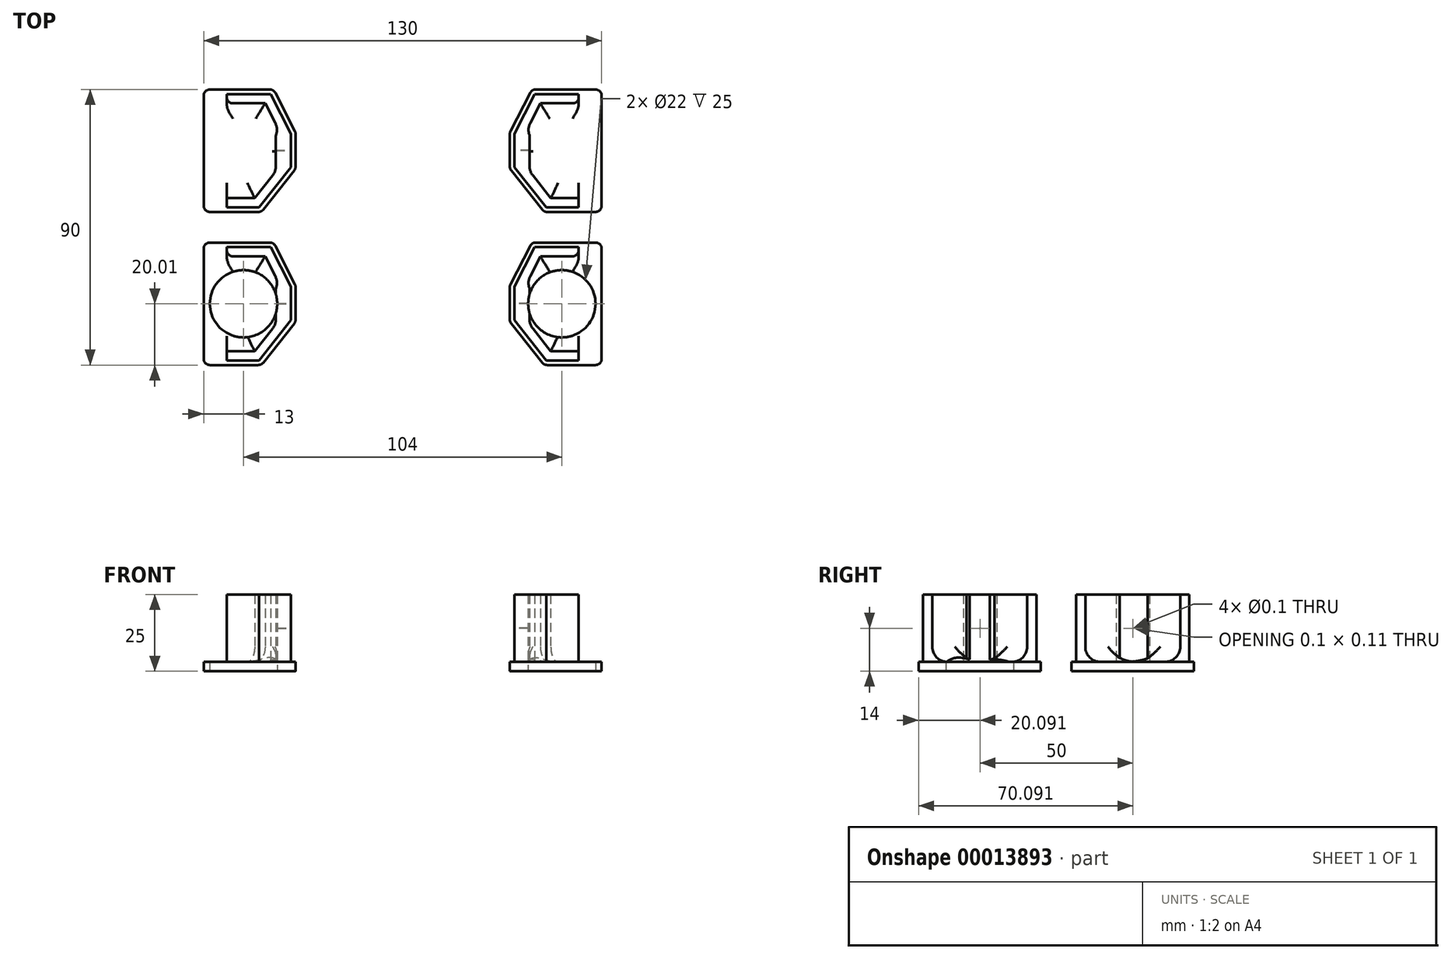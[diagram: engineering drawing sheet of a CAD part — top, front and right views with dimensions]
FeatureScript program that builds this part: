
annotation { "Feature Type Name" : "Feature", "Feature Type Description" : "" }
export const myFeature = defineFeature(function(context is Context, id is Id, definition is map)
    precondition{}
    {
        {
            var Q0;
            Q0=qCreatedBy(makeId("Right.planeOp"),FACE);
            var sketch = newSketch(context, id + "F0", { "sketchPlane" : qUnion([Q0])});
            skLineSegment(sketch, "E0", {"start": v(-20.01, 30) * mm, "end": v(-20.01, 11.2) * mm});
            skLineSegment(sketch, "E1", {"start": v(-20.01, 11.2) * mm, "end": v(-5.9, 0) * mm});
            skLineSegment(sketch, "E2", {"start": v(-5.9, 0) * mm, "end": v(5.9, 0) * mm});
            skLineSegment(sketch, "E3", {"start": v(5.9, 0) * mm, "end": v(20, 7.2) * mm});
            skLineSegment(sketch, "E4", {"start": v(20, 7.2) * mm, "end": v(19.99, 30) * mm});
            skLineSegment(sketch, "E5", {"start": v(19.99, 30) * mm, "end": v(18.49, 30) * mm});
            skLineSegment(sketch, "E6", {"start": v(18.49, 30) * mm, "end": v(18.49, 28.6) * mm});
            skLineSegment(sketch, "E7", {"start": v(18.49, 28.6) * mm, "end": v(17.7, 28.6) * mm});
            skLineSegment(sketch, "E8", {"start": v(17.7, 28.6) * mm, "end": v(16.3, 24.7) * mm});
            skLineSegment(sketch, "E9", {"start": v(18.49, 22.5) * mm, "end": v(18.49, 8.12) * mm});
            skLineSegment(sketch, "E10", {"start": v(18.49, 8.12) * mm, "end": v(5.54, 1.5) * mm});
            skLineSegment(sketch, "E11", {"start": v(5.54, 1.5) * mm, "end": v(-5.38, 1.5) * mm});
            skLineSegment(sketch, "E12", {"start": v(-5.38, 1.5) * mm, "end": v(-18.5, 11.92) * mm});
            skLineSegment(sketch, "E13", {"start": v(-18.5, 22.5) * mm, "end": v(-16.31, 24.7) * mm});
            skLineSegment(sketch, "E14", {"start": v(-16.31, 24.7) * mm, "end": v(-17.73, 28.6) * mm});
            skLineSegment(sketch, "E15", {"start": v(-17.73, 28.6) * mm, "end": v(-18.5, 28.6) * mm});
            skLineSegment(sketch, "E16", {"start": v(-18.5, 28.6) * mm, "end": v(-18.5, 30) * mm});
            skLineSegment(sketch, "E17", {"start": v(-18.5, 30) * mm, "end": v(-20.01, 30) * mm});
            skLineSegment(sketch, "E18", {"start": v(-16.31, 10.1) * mm, "end": v(-16.31, 24.7) * mm, "construction": true});
            skLineSegment(sketch, "E19", {"start": v(-18.5, 22.5) * mm, "end": v(18.49, 22.5) * mm});
            skLineSegment(sketch, "E20", {"start": v(-18.5, 22.5) * mm, "end": v(-18.5, 11.92) * mm});
            skLineSegment(sketch, "E21", {"start": v(-20.01, 30) * mm, "end": v(19.99, 30) * mm});
            skLineSegment(sketch, "E22", {"start": v(-18.5, 28.6) * mm, "end": v(18.49, 28.6) * mm, "construction": true});
            skLineSegment(sketch, "E23", {"start": v(16.29, 24.7) * mm, "end": v(18.49, 22.5) * mm});
            skLineSegment(sketch, "E24", {"start": v(-16.31, 24.7) * mm, "end": v(16.3, 24.7) * mm, "construction": true});
            skLineSegment(sketch, "E25", {"start": v(-0.01, 24.7) * mm, "end": v(-0.01, 30) * mm, "construction": true});
            skPoint(sketch, "E26", {"position": v(0, 0) * mm});
            skSolve(sketch);
        }
        {
            var Q0;
            {var subQ4=sQuery(id+"F0.wireOp",EDGE,"E0");Q0=makeQuery(id+"F0.imprint","IMPRINT",FACE,{"disambiguationData":[TD([[makeQuery(id+"F0.imprint","IMPRINT",EDGE,{"derivedFrom":subQ4}),1.0]])]});}
            var Q1;
            {var subQ2=sQuery(id+"F0.wireOp",EDGE,"E6");Q1=makeQuery(id+"F0.imprint","IMPRINT",FACE,{"disambiguationData":[TD([[makeQuery(id+"F0.imprint","IMPRINT",EDGE,{"derivedFrom":subQ2}),-1.0]])]});}
            var Q2;
            Q2=makeQuery(id+"F0.imprint","IMPRINT",FACE,{"disambiguationData":[TD([[makeQuery(id+"F0.imprint","IMPRINT",EDGE,{"derivedFrom":sQuery(id+"F0.wireOp",EDGE,"E9")}),-1.0]])]});
            extrude(context, id + "F1", {"entities" : qUnion([Q0, Q1, Q2]), "depth" : 3 * mm});
        }
        {
            var Q0;
            Q0=makeQuery(id+"F0.imprint","IMPRINT",FACE,{"disambiguationData":[TD([[makeQuery(id+"F0.imprint","IMPRINT",EDGE,{"derivedFrom":sQuery(id+"F0.wireOp",EDGE,"E9")}),-1.0]])]});
            extrude(context, id + "F2", {"entities" : qUnion([Q0]), "operationType" : NewBodyOperationType.ADD, "oppositeDirection" : true, "depth" : 22 * mm});
        }
        {
            var Q0;
            Q0=makeQuery(id+"F2.opExtrude","CAP_FACE",FACE,{"disambiguationData":[OSD([sQuery(id+"F0.wireOp",EDGE,"E9"),sQuery(id+"F0.wireOp",EDGE,"E10"),sQuery(id+"F0.wireOp",EDGE,"E11"),sQuery(id+"F0.wireOp",EDGE,"E12"),sQuery(id+"F0.wireOp",EDGE,"E19"),sQuery(id+"F0.wireOp",EDGE,"E20")])],"isStart":false});
            shell(context, id + "F3", {"entities" : qUnion([Q0]), "thickness" : 3 * mm});
        }
        {
            var Q0;
            Q0=makeQuery(id+"F3.opShell","OFFSET_FACE",FACE,{"disambiguationData":[OSD([sQuery(id+"F0.wireOp",EDGE,"E19")])]});
            extrude(context, id + "F4", {"entities" : qUnion([Q0]), "operationType" : NewBodyOperationType.REMOVE, "endBound" : BoundingType.UP_TO_NEXT, "oppositeDirection" : true, "depth" : 25 * mm});
        }
        {
            var Q0;
            Q0=makeQuery(id+"F2.opExtrude","SWEPT_FACE",FACE,{"disambiguationData":[OSD([sQuery(id+"F0.wireOp",EDGE,"E11")])]});
            var sketch = newSketch(context, id + "F5", { "sketchPlane" : qUnion([Q0])});
            skLineSegment(sketch, "E27", {"start": v(-11, 5.38) * mm, "end": v(-11, -5.54) * mm, "construction": true});
            skPoint(sketch, "E28", {"position": v(-11, -0.08) * mm});
            skSolve(sketch);
        }
        {
            var Q0;
            Q0=sQuery(id+"F5.wireOp",VERTEX,"E28");
            var Q1;
            Q1=makeQuery(id+"F1.opExtrude","SWEPT_BODY",BODY,{"disambiguationData":[OSD([sQuery(id+"F0.wireOp",EDGE,"E0"),sQuery(id+"F0.wireOp",EDGE,"E1"),sQuery(id+"F0.wireOp",EDGE,"E2"),sQuery(id+"F0.wireOp",EDGE,"E3"),sQuery(id+"F0.wireOp",EDGE,"E4"),sQuery(id+"F0.wireOp",EDGE,"E21")])]});
            hole(context, id + "F6", {"style" : HoleStyle.SIMPLE, "holeDiameter" : 1 / 203.2 * mm + 0.1 * mm, "endStyle" : HoleEndStyle.THROUGH, "locations" : qUnion([Q0]), "scope" : qUnion([Q1]), "isTappedThrough" : true});
        }
        {
            var Q0;
            Q0=makeQuery(id+"F3.opShell","OFFSET_FACE",FACE,{"disambiguationData":[OSD([sQuery(id+"F0.wireOp",EDGE,"E11")])]});
            extrude(context, id + "F7", {"entities" : qUnion([Q0]), "operationType" : NewBodyOperationType.ADD, "depth" : 2 * mm});
        }
        {
            var Q0;
            {var subQ0=sQuery(id+"F0.wireOp",EDGE,"E21");var subQ1=sQuery(id+"F0.wireOp",EDGE,"E9");var subQ2=sQuery(id+"F0.wireOp",EDGE,"E4");var subQ3=sQuery(id+"F0.wireOp",EDGE,"E3");var subQ4=sQuery(id+"F0.wireOp",EDGE,"E2");var subQ5=sQuery(id+"F0.wireOp",EDGE,"E1");var subQ6=sQuery(id+"F0.wireOp",EDGE,"E0");Q0=makeQuery(id+"F4.boolean.opBoolean","MERGE",EDGE,{"derivedFrom":[makeQuery(id+"F3.opShell","TWEAK_EDGE",EDGE,{"derivedFrom":[makeQuery(id+"F1.opExtrude","CAP_FACE",FACE,{"disambiguationData":[OSD([subQ6,subQ5,subQ4,subQ3,subQ2,subQ0])],"isStart":false}),makeQuery(id+"F2.opExtrude","SWEPT_FACE",FACE,{"disambiguationData":[OSD([subQ1])]})]})],"fromTools":[makeQuery(id+"F4.opExtrude","SWEPT_EDGE",EDGE,{"disambiguationData":[OSD([subQ6,subQ5,subQ4,subQ3,subQ2,subQ1,sQuery(id+"F0.wireOp",EDGE,"E19"),subQ0])]})]});}
            var Q1;
            Q1=makeQuery(id+"F3.opShell","TWEAK_EDGE",EDGE,{"derivedFrom":[makeQuery(id+"F1.opExtrude","CAP_FACE",FACE,{"disambiguationData":[OSD([sQuery(id+"F0.wireOp",EDGE,"E0"),sQuery(id+"F0.wireOp",EDGE,"E1"),sQuery(id+"F0.wireOp",EDGE,"E2"),sQuery(id+"F0.wireOp",EDGE,"E3"),sQuery(id+"F0.wireOp",EDGE,"E4"),sQuery(id+"F0.wireOp",EDGE,"E21")])],"isStart":false}),makeQuery(id+"F2.opExtrude","SWEPT_FACE",FACE,{"disambiguationData":[OSD([sQuery(id+"F0.wireOp",EDGE,"E10")])]})]});
            var Q2;
            Q2=makeQuery(id+"F3.opShell","TWEAK_EDGE",EDGE,{"derivedFrom":[makeQuery(id+"F1.opExtrude","CAP_FACE",FACE,{"disambiguationData":[OSD([sQuery(id+"F0.wireOp",EDGE,"E0"),sQuery(id+"F0.wireOp",EDGE,"E1"),sQuery(id+"F0.wireOp",EDGE,"E2"),sQuery(id+"F0.wireOp",EDGE,"E3"),sQuery(id+"F0.wireOp",EDGE,"E4"),sQuery(id+"F0.wireOp",EDGE,"E21")])],"isStart":false}),makeQuery(id+"F2.opExtrude","SWEPT_FACE",FACE,{"disambiguationData":[OSD([sQuery(id+"F0.wireOp",EDGE,"E11")])]})]});
            var Q3;
            Q3=makeQuery(id+"F3.opShell","TWEAK_EDGE",EDGE,{"derivedFrom":[makeQuery(id+"F1.opExtrude","CAP_FACE",FACE,{"disambiguationData":[OSD([sQuery(id+"F0.wireOp",EDGE,"E0"),sQuery(id+"F0.wireOp",EDGE,"E1"),sQuery(id+"F0.wireOp",EDGE,"E2"),sQuery(id+"F0.wireOp",EDGE,"E3"),sQuery(id+"F0.wireOp",EDGE,"E4"),sQuery(id+"F0.wireOp",EDGE,"E21")])],"isStart":false}),makeQuery(id+"F2.opExtrude","SWEPT_FACE",FACE,{"disambiguationData":[OSD([sQuery(id+"F0.wireOp",EDGE,"E12")])]})]});
            var Q4;
            {var subQ0=sQuery(id+"F0.wireOp",EDGE,"E21");var subQ1=sQuery(id+"F0.wireOp",EDGE,"E20");var subQ2=sQuery(id+"F0.wireOp",EDGE,"E4");var subQ3=sQuery(id+"F0.wireOp",EDGE,"E3");var subQ4=sQuery(id+"F0.wireOp",EDGE,"E2");var subQ5=sQuery(id+"F0.wireOp",EDGE,"E1");var subQ6=sQuery(id+"F0.wireOp",EDGE,"E0");Q4=makeQuery(id+"F4.boolean.opBoolean","MERGE",EDGE,{"derivedFrom":[makeQuery(id+"F3.opShell","TWEAK_EDGE",EDGE,{"derivedFrom":[makeQuery(id+"F1.opExtrude","CAP_FACE",FACE,{"disambiguationData":[OSD([subQ6,subQ5,subQ4,subQ3,subQ2,subQ0])],"isStart":false}),makeQuery(id+"F2.opExtrude","SWEPT_FACE",FACE,{"disambiguationData":[OSD([subQ1])]})]})],"fromTools":[makeQuery(id+"F4.opExtrude","SWEPT_EDGE",EDGE,{"disambiguationData":[OSD([subQ6,subQ5,subQ4,subQ3,subQ2,sQuery(id+"F0.wireOp",EDGE,"E19"),subQ1,subQ0])]})]});}
            fillet(context, id + "F8", {"entities" : qUnion([Q0, Q1, Q2, Q3, Q4]), "radius" : 5 * mm, "tangentPropagation" : true, "allowEdgeOverflow" : false});
        }
        {
            var Q0;
            Q0=makeQuery(id+"F4.boolean.opBoolean","COPY",EDGE,{"derivedFrom":makeQuery(id+"F4.opExtrude","CAP_EDGE",EDGE,{"disambiguationData":[OSD([sQuery(id+"F0.wireOp",EDGE,"E9"),sQuery(id+"F0.wireOp",EDGE,"E19"),sQuery(id+"F0.wireOp",EDGE,"E23")])],"isStart":false})});
            var Q1;
            Q1=makeQuery(id+"F4.boolean.opBoolean","COPY",EDGE,{"derivedFrom":makeQuery(id+"F4.opExtrude","CAP_EDGE",EDGE,{"disambiguationData":[OSD([sQuery(id+"F0.wireOp",EDGE,"E13"),sQuery(id+"F0.wireOp",EDGE,"E19"),sQuery(id+"F0.wireOp",EDGE,"E20")])],"isStart":false})});
            fillet(context, id + "F9", {"entities" : qUnion([Q0, Q1]), "radius" : 2 * mm, "tangentPropagation" : true, "allowEdgeOverflow" : false});
        }
        {
            var Q0;
            {var subQ0=sQuery(id+"F0.wireOp",EDGE,"E11");var subQ1=sQuery(id+"F0.wireOp",EDGE,"E10");Q0=makeQuery(id+"F7.boolean.opBoolean","MERGE",EDGE,{"derivedFrom":[makeQuery(id+"F3.opShell","OFFSET_EDGE",EDGE,{"disambiguationData":[OSD([subQ1,subQ0])]}),makeQuery(id+"F7.opExtrude","CAP_EDGE",EDGE,{"disambiguationData":[OSD([subQ1,subQ0])],"isStart":true})]});}
            var Q1;
            {var subQ0=sQuery(id+"F0.wireOp",EDGE,"E12");var subQ1=sQuery(id+"F0.wireOp",EDGE,"E11");Q1=makeQuery(id+"F7.boolean.opBoolean","MERGE",EDGE,{"derivedFrom":[makeQuery(id+"F3.opShell","OFFSET_EDGE",EDGE,{"disambiguationData":[OSD([subQ1,subQ0])]}),makeQuery(id+"F7.opExtrude","CAP_EDGE",EDGE,{"disambiguationData":[OSD([subQ1,subQ0])],"isStart":true})]});}
            fillet(context, id + "F10", {"entities" : qUnion([Q0, Q1]), "radius" : 5 * mm, "tangentPropagation" : true, "allowEdgeOverflow" : false});
        }
        {
            var Q0;
            Q0=makeQuery(id+"F2.opExtrude","CAP_FACE",FACE,{"disambiguationData":[OSD([sQuery(id+"F0.wireOp",EDGE,"E9"),sQuery(id+"F0.wireOp",EDGE,"E10"),sQuery(id+"F0.wireOp",EDGE,"E11"),sQuery(id+"F0.wireOp",EDGE,"E12"),sQuery(id+"F0.wireOp",EDGE,"E19"),sQuery(id+"F0.wireOp",EDGE,"E20")])],"isStart":false});
            cPlane(context, id + "F11", {"entities" : qUnion([Q0]), "cplaneType" : CPlaneType.OFFSET, "offset" : 10 * mm, "width" : 150 * mm, "height" : 150 * mm});
        }
        {
            var Q0;
            Q0=makeQuery(id+"F1.opExtrude","CAP_FACE",FACE,{"disambiguationData":[OSD([sQuery(id+"F0.wireOp",EDGE,"E0"),sQuery(id+"F0.wireOp",EDGE,"E1"),sQuery(id+"F0.wireOp",EDGE,"E2"),sQuery(id+"F0.wireOp",EDGE,"E3"),sQuery(id+"F0.wireOp",EDGE,"E4"),sQuery(id+"F0.wireOp",EDGE,"E21")])],"isStart":false});
            var sketch = newSketch(context, id + "F12", { "sketchPlane" : qUnion([Q0])});
            skCircle(sketch, "E29", {"center": v(0, 17) * mm, "radius": 11 * mm});
            skSolve(sketch);
        }
        {
            var Q0;
            Q0=makeQuery(id+"F1.opExtrude","SWEPT_EDGE",EDGE,{"disambiguationData":[OSD([sQuery(id+"F0.wireOp",EDGE,"E4"),sQuery(id+"F0.wireOp",EDGE,"E21")])]});
            var Q1;
            Q1=makeQuery(id+"F1.opExtrude","SWEPT_EDGE",EDGE,{"disambiguationData":[OSD([sQuery(id+"F0.wireOp",EDGE,"E3"),sQuery(id+"F0.wireOp",EDGE,"E4")])]});
            var Q2;
            Q2=makeQuery(id+"F1.opExtrude","SWEPT_EDGE",EDGE,{"disambiguationData":[OSD([sQuery(id+"F0.wireOp",EDGE,"E2"),sQuery(id+"F0.wireOp",EDGE,"E3")])]});
            var Q3;
            Q3=makeQuery(id+"F1.opExtrude","SWEPT_EDGE",EDGE,{"disambiguationData":[OSD([sQuery(id+"F0.wireOp",EDGE,"E1"),sQuery(id+"F0.wireOp",EDGE,"E2")])]});
            var Q4;
            Q4=makeQuery(id+"F1.opExtrude","SWEPT_EDGE",EDGE,{"disambiguationData":[OSD([sQuery(id+"F0.wireOp",EDGE,"E0"),sQuery(id+"F0.wireOp",EDGE,"E1")])]});
            var Q5;
            Q5=makeQuery(id+"F1.opExtrude","SWEPT_EDGE",EDGE,{"disambiguationData":[OSD([sQuery(id+"F0.wireOp",EDGE,"E0"),sQuery(id+"F0.wireOp",EDGE,"E21")])]});
            fillet(context, id + "F13", {"entities" : qUnion([Q0, Q1, Q2, Q3, Q4, Q5]), "radius" : 2 * mm, "tangentPropagation" : true, "allowEdgeOverflow" : false});
        }
        {
            var Q0;
            Q0=makeQuery(id+"F1.opExtrude","SWEPT_BODY",BODY,{"disambiguationData":[OSD([sQuery(id+"F0.wireOp",EDGE,"E0"),sQuery(id+"F0.wireOp",EDGE,"E1"),sQuery(id+"F0.wireOp",EDGE,"E2"),sQuery(id+"F0.wireOp",EDGE,"E3"),sQuery(id+"F0.wireOp",EDGE,"E4"),sQuery(id+"F0.wireOp",EDGE,"E21")])]});
            var Q1;
            Q1=makeQuery(id+"F16.opPattern","COPY",BODY,{"derivedFrom":makeQuery(id+"F1.opExtrude","SWEPT_BODY",BODY,{"disambiguationData":[OSD([sQuery(id+"F0.wireOp",EDGE,"E0"),sQuery(id+"F0.wireOp",EDGE,"E1"),sQuery(id+"F0.wireOp",EDGE,"E2"),sQuery(id+"F0.wireOp",EDGE,"E3"),sQuery(id+"F0.wireOp",EDGE,"E4"),sQuery(id+"F0.wireOp",EDGE,"E21")])]}),"instanceName":"1"});
            transform(context, id + "F14", {"entities" : qUnion([Q0, Q1]), "transformType" : TransformType.TRANSLATION_3D, "dx" : 0 * mm, "dy" : 50 * mm, "dz" : 0 * mm, "makeCopy" : true});
        }
        {
            var Q0;
            Q0=makeQuery(id+"F12.imprint","IMPRINT",FACE,{"disambiguationData":[TD([[makeQuery(id+"F12.imprint","IMPRINT",EDGE,{"derivedFrom":sQuery(id+"F12.wireOp",EDGE,"E29")}),1.0]])]});
            extrude(context, id + "F15", {"entities" : qUnion([Q0]), "operationType" : NewBodyOperationType.REMOVE, "endBound" : BoundingType.UP_TO_NEXT, "oppositeDirection" : true, "depth" : 25 * mm});
        }
        {
            var Q0;
            Q0=makeQuery(id+"F1.opExtrude","SWEPT_BODY",BODY,{"disambiguationData":[OSD([sQuery(id+"F0.wireOp",EDGE,"E0"),sQuery(id+"F0.wireOp",EDGE,"E1"),sQuery(id+"F0.wireOp",EDGE,"E2"),sQuery(id+"F0.wireOp",EDGE,"E3"),sQuery(id+"F0.wireOp",EDGE,"E4"),sQuery(id+"F0.wireOp",EDGE,"E21")])]});
            var Q1;
            Q1=qCreatedBy(id+"F11.planeOp",FACE);
            mirror(context, id + "F16", {"entities" : qUnion([Q0]), "mirrorPlane" : qUnion([Q1])});
        }
        {
            var Q0;
            Q0=makeQuery(id+"F14.opPattern","COPY",BODY,{"derivedFrom":makeQuery(id+"F1.opExtrude","SWEPT_BODY",BODY,{"disambiguationData":[OSD([sQuery(id+"F0.wireOp",EDGE,"E0"),sQuery(id+"F0.wireOp",EDGE,"E1"),sQuery(id+"F0.wireOp",EDGE,"E2"),sQuery(id+"F0.wireOp",EDGE,"E3"),sQuery(id+"F0.wireOp",EDGE,"E4"),sQuery(id+"F0.wireOp",EDGE,"E21")])]}),"instanceName":"1"});
            var Q1;
            Q1=qCreatedBy(id+"F11.planeOp",FACE);
            mirror(context, id + "F17", {"entities" : qUnion([Q0]), "mirrorPlane" : qUnion([Q1])});
        }
        {
            var Q0;
            Q0=makeQuery(id+"F1.opExtrude","SWEPT_BODY",BODY,{"disambiguationData":[OSD([sQuery(id+"F0.wireOp",EDGE,"E0"),sQuery(id+"F0.wireOp",EDGE,"E1"),sQuery(id+"F0.wireOp",EDGE,"E2"),sQuery(id+"F0.wireOp",EDGE,"E3"),sQuery(id+"F0.wireOp",EDGE,"E4"),sQuery(id+"F0.wireOp",EDGE,"E21")])]});
            var Q1;
            Q1=makeQuery(id+"F14.opPattern","COPY",BODY,{"derivedFrom":makeQuery(id+"F1.opExtrude","SWEPT_BODY",BODY,{"disambiguationData":[OSD([sQuery(id+"F0.wireOp",EDGE,"E0"),sQuery(id+"F0.wireOp",EDGE,"E1"),sQuery(id+"F0.wireOp",EDGE,"E2"),sQuery(id+"F0.wireOp",EDGE,"E3"),sQuery(id+"F0.wireOp",EDGE,"E4"),sQuery(id+"F0.wireOp",EDGE,"E21")])]}),"instanceName":"1"});
            var Q2;
            Q2=makeQuery(id+"F1.opExtrude","CAP_EDGE",EDGE,{"disambiguationData":[OSD([sQuery(id+"F0.wireOp",EDGE,"E2")])],"isStart":false});
            transform(context, id + "F18", {"entities" : qUnion([Q0, Q1]), "transformType" : TransformType.ROTATION, "transformAxis" : qUnion([Q2]), "angle" : 90 * degree, "makeCopy" : false});
        }
        {
            var Q0;
            Q0=makeQuery(id+"F17.opPattern","COPY",BODY,{"derivedFrom":makeQuery(id+"F14.opPattern","COPY",BODY,{"derivedFrom":makeQuery(id+"F1.opExtrude","SWEPT_BODY",BODY,{"disambiguationData":[OSD([sQuery(id+"F0.wireOp",EDGE,"E0"),sQuery(id+"F0.wireOp",EDGE,"E1"),sQuery(id+"F0.wireOp",EDGE,"E2"),sQuery(id+"F0.wireOp",EDGE,"E3"),sQuery(id+"F0.wireOp",EDGE,"E4"),sQuery(id+"F0.wireOp",EDGE,"E21")])]}),"instanceName":"1"}),"instanceName":"1"});
            var Q1;
            Q1=makeQuery(id+"F16.opPattern","COPY",BODY,{"derivedFrom":makeQuery(id+"F1.opExtrude","SWEPT_BODY",BODY,{"disambiguationData":[OSD([sQuery(id+"F0.wireOp",EDGE,"E0"),sQuery(id+"F0.wireOp",EDGE,"E1"),sQuery(id+"F0.wireOp",EDGE,"E2"),sQuery(id+"F0.wireOp",EDGE,"E3"),sQuery(id+"F0.wireOp",EDGE,"E4"),sQuery(id+"F0.wireOp",EDGE,"E21")])]}),"instanceName":"1"});
            var Q2;
            Q2=makeQuery(id+"F17.opPattern","COPY",EDGE,{"derivedFrom":makeQuery(id+"F14.opPattern","COPY",EDGE,{"derivedFrom":makeQuery(id+"F1.opExtrude","CAP_EDGE",EDGE,{"disambiguationData":[OSD([sQuery(id+"F0.wireOp",EDGE,"E2")])],"isStart":false}),"instanceName":"1"}),"instanceName":"1"});
            transform(context, id + "F19", {"entities" : qUnion([Q0, Q1]), "transformType" : TransformType.ROTATION, "transformAxis" : qUnion([Q2]), "angle" : 270 * degree, "makeCopy" : false});
        }
    });
